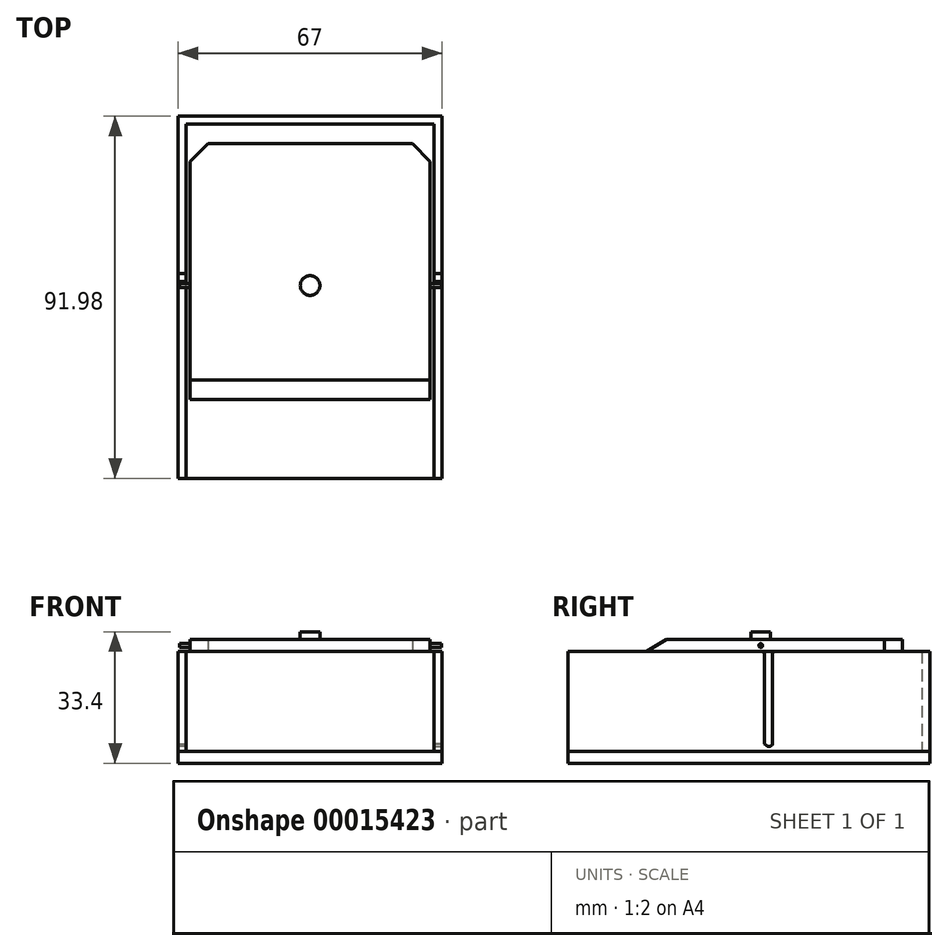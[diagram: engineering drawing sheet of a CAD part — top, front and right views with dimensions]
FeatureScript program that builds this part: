
annotation { "Feature Type Name" : "Feature", "Feature Type Description" : "" }
export const myFeature = defineFeature(function(context is Context, id is Id, definition is map)
    precondition{}
    {
        {
            var Q0;
            Q0=qCreatedBy(makeId("Top.planeOp"),FACE);
            var sketch = newSketch(context, id + "F0", { "sketchPlane" : qUnion([Q0])});
            skLineSegment(sketch, "E0.bottom", {"start": v(-39.88, -77.5) * mm, "end": v(23.12, -77.5) * mm});
            skLineSegment(sketch, "E0.top", {"start": v(-39.88, 12.5) * mm, "end": v(23.12, 12.5) * mm});
            skLineSegment(sketch, "E0.left", {"start": v(-39.88, -77.5) * mm, "end": v(-39.88, 12.5) * mm});
            skLineSegment(sketch, "E0.right", {"start": v(23.12, -77.5) * mm, "end": v(23.12, 12.5) * mm});
            skLineSegment(sketch, "E1.bottom", {"start": v(-41.88, -77.48) * mm, "end": v(25.12, -77.48) * mm});
            skLineSegment(sketch, "E1.top", {"start": v(-41.88, 14.5) * mm, "end": v(25.12, 14.5) * mm});
            skLineSegment(sketch, "E1.left", {"start": v(-41.88, -77.48) * mm, "end": v(-41.88, 14.5) * mm});
            skLineSegment(sketch, "E1.right", {"start": v(25.12, -77.48) * mm, "end": v(25.12, 14.5) * mm});
            skSolve(sketch);
        }
        {
            var Q0;
            {var subQ7=sQuery(id+"F0.wireOp",EDGE,"E0.top");Q0=makeQuery(id+"F0.imprint","IMPRINT",FACE,{"disambiguationData":[TD([[makeQuery(id+"F0.imprint","IMPRINT",EDGE,{"derivedFrom":subQ7}),1.0]])]});}
            extrude(context, id + "F1", {"entities" : qUnion([Q0]), "depth" : 25.4 * mm});
        }
        {
            var Q0;
            Q0=makeQuery(id+"F1.opExtrude","SWEPT_FACE",FACE,{"disambiguationData":[OSD([sQuery(id+"F0.wireOp",EDGE,"E0.left")])]});
            var sketch = newSketch(context, id + "F2", { "sketchPlane" : qUnion([Q0])});
            skLineSegment(sketch, "E2", {"start": v(-25.5, 25.4) * mm, "end": v(-25.5, 1.76) * mm});
            skLineSegment(sketch, "E3", {"start": v(-25.5, 1.76) * mm, "end": v(-26.4, 0.86) * mm});
            skLineSegment(sketch, "E4", {"start": v(-26.4, 0.86) * mm, "end": v(-27.5, 1.96) * mm});
            skLineSegment(sketch, "E5", {"start": v(-27.5, 1.96) * mm, "end": v(-27.5, 25.4) * mm});
            skLineSegment(sketch, "E6", {"start": v(-27.5, 25.4) * mm, "end": v(-25.5, 25.4) * mm});
            skSolve(sketch);
        }
        {
            var Q0;
            Q0=makeQuery(id+"F2.imprint","IMPRINT",FACE,{"disambiguationData":[TD([[makeQuery(id+"F2.imprint","IMPRINT",EDGE,{"derivedFrom":sQuery(id+"F2.wireOp",EDGE,"E2")}),-1.0]])]});
            extrude(context, id + "F3", {"entities" : qUnion([Q0]), "operationType" : NewBodyOperationType.REMOVE, "oppositeDirection" : true, "depth" : 2.03 * mm});
        }
        {
            var Q0;
            Q0=qSketchRegion(id+"F2",true);
            var Q1;
            Q1=makeQuery(id+"F2.imprint","IMPRINT",FACE,{"disambiguationData":[TD([[makeQuery(id+"F2.imprint","IMPRINT",EDGE,{"derivedFrom":sQuery(id+"F2.wireOp",EDGE,"E2")}),-1.0]])]});
            extrude(context, id + "F4", {"entities" : qUnion([Q0, Q1]), "operationType" : NewBodyOperationType.REMOVE, "depth" : 77.17 * mm});
        }
        {
            var Q0;
            {var subQ0=sQuery(id+"F0.wireOp",EDGE,"E0.top");var subQ1=sQuery(id+"F0.wireOp",EDGE,"E0.left");var subQ2=sQuery(id+"F0.wireOp",EDGE,"E0.right");var subQ3=sQuery(id+"F0.wireOp",EDGE,"E1.bottom");var subQ4=sQuery(id+"F0.wireOp",EDGE,"E1.top");var subQ5=sQuery(id+"F0.wireOp",EDGE,"E1.left");var subQ6=sQuery(id+"F0.wireOp",EDGE,"E1.right");var subQ14=makeQuery(id+"F1.opExtrude","SWEPT_FACE",FACE,{"disambiguationData":[OSD([subQ0])]});Q0=makeQuery(id+"F4.boolean.opBoolean","SPLIT",FACE,{"disambiguationData":[TD([subQ14])],"derivedFrom":makeQuery(id+"F3.boolean.opBoolean","SPLIT",FACE,{"disambiguationData":[TD([subQ14])],"derivedFrom":makeQuery(id+"F1.opExtrude","CAP_FACE",FACE,{"disambiguationData":[OSD([subQ0,subQ1,subQ2,subQ3,subQ4,subQ5,subQ6])],"isStart":false})})});}
            var sketch = newSketch(context, id + "F5", { "sketchPlane" : qUnion([Q0])});
            skLineSegment(sketch, "E7", {"start": v(-34.36, 7.5) * mm, "end": v(-38.88, 2.99) * mm});
            skLineSegment(sketch, "E8", {"start": v(-38.88, 2.99) * mm, "end": v(-38.88, -57.48) * mm});
            skLineSegment(sketch, "E9", {"start": v(-38.88, -57.48) * mm, "end": v(22.12, -57.48) * mm});
            skLineSegment(sketch, "E10", {"start": v(22.12, -57.48) * mm, "end": v(22.12, 2.99) * mm});
            skLineSegment(sketch, "E11", {"start": v(22.12, 2.99) * mm, "end": v(17.6, 7.5) * mm});
            skLineSegment(sketch, "E12", {"start": v(17.6, 7.5) * mm, "end": v(-34.36, 7.5) * mm});
            skSolve(sketch);
        }
        {
            var Q0;
            Q0=makeQuery(id+"F5.imprint","IMPRINT",FACE,{"disambiguationData":[TD([[makeQuery(id+"F5.imprint","IMPRINT",EDGE,{"derivedFrom":sQuery(id+"F5.wireOp",EDGE,"E7")}),1.0]])]});
            extrude(context, id + "F6", {"entities" : qUnion([Q0]), "depth" : 3 * mm});
        }
        {
            var Q0;
            Q0=makeQuery(id+"F6.opExtrude","SWEPT_FACE",FACE,{"disambiguationData":[OSD([sQuery(id+"F5.wireOp",EDGE,"E10")])]});
            var sketch = newSketch(context, id + "F7", { "sketchPlane" : qUnion([Q0])});
            skCircle(sketch, "E13", {"center": v(-28.5, 26.9) * mm, "radius": 0.48 * mm});
            skSolve(sketch);
        }
        {
            var Q0;
            Q0=makeQuery(id+"F7.imprint","IMPRINT",FACE,{"disambiguationData":[TD([[makeQuery(id+"F7.imprint","IMPRINT",EDGE,{"derivedFrom":sQuery(id+"F7.wireOp",EDGE,"E13")}),1.0]])]});
            extrude(context, id + "F8", {"entities" : qUnion([Q0]), "operationType" : NewBodyOperationType.ADD, "depth" : 2.88 * mm});
        }
        {
            var Q0;
            Q0=makeQuery(id+"F8.opExtrude","CAP_FACE",FACE,{"disambiguationData":[OSD([sQuery(id+"F7.wireOp",EDGE,"E13")])],"isStart":false});
            extrude(context, id + "F9", {"entities" : qUnion([Q0]), "operationType" : NewBodyOperationType.ADD, "oppositeDirection" : true, "depth" : 66.56 * mm});
        }
        {
            var Q0;
            {var subQ5=sQuery(id+"F0.wireOp",EDGE,"E0.top");Q0=makeQuery(id+"F0.imprint","IMPRINT",FACE,{"disambiguationData":[TD([[makeQuery(id+"F0.imprint","IMPRINT",EDGE,{"derivedFrom":subQ5}),-1.0]])]});}
            var Q1;
            {var subQ7=sQuery(id+"F0.wireOp",EDGE,"E0.top");Q1=makeQuery(id+"F0.imprint","IMPRINT",FACE,{"disambiguationData":[TD([[makeQuery(id+"F0.imprint","IMPRINT",EDGE,{"derivedFrom":subQ7}),1.0]])]});}
            extrude(context, id + "F10", {"entities" : qUnion([Q0, Q1]), "oppositeDirection" : true, "depth" : 3 * mm});
        }
        {
            var Q0;
            Q0=makeQuery(id+"F6.opExtrude","CAP_FACE",FACE,{"disambiguationData":[OSD([sQuery(id+"F5.wireOp",EDGE,"E7"),sQuery(id+"F5.wireOp",EDGE,"E8"),sQuery(id+"F5.wireOp",EDGE,"E9"),sQuery(id+"F5.wireOp",EDGE,"E10"),sQuery(id+"F5.wireOp",EDGE,"E11"),sQuery(id+"F5.wireOp",EDGE,"E12")])],"isStart":false});
            var sketch = newSketch(context, id + "F11", { "sketchPlane" : qUnion([Q0])});
            skPoint(sketch, "E14", {"position": v(-38.88, -28.5) * mm});
            skPoint(sketch, "E15", {"position": v(22.12, -28.5) * mm});
            skLineSegment(sketch, "E16", {"start": v(-38.88, -28.5) * mm, "end": v(-8.38, -28.5) * mm});
            skLineSegment(sketch, "E17", {"start": v(-8.38, -28.5) * mm, "end": v(22.12, -28.5) * mm});
            skCircle(sketch, "E18", {"center": v(-8.38, -28.5) * mm, "radius": 2.5 * mm});
            skCircle(sketch, "E19", {"center": v(-8.38, -28.5) * mm, "radius": 3.57 * mm});
            skSolve(sketch);
        }
        {
            var Q0;
            {var subQ1=sQuery(id+"F11.wireOp",EDGE,"E17");var subQ3=sQuery(id+"F11.wireOp",EDGE,"E16");var subQ5=makeQuery(id+"F11.imprint","INTERSECT",VERTEX,{"derivedFrom":[subQ3,subQ1]});Q0=makeQuery(id+"F11.imprint","IMPRINT",FACE,{"disambiguationData":[TD([[makeQuery(id+"F11.imprint","IMPRINT",EDGE,{"disambiguationData":[TD([[subQ5,1.0]])],"derivedFrom":subQ3}),1.0]])]});}
            var Q1;
            {var subQ1=sQuery(id+"F11.wireOp",EDGE,"E17");var subQ3=sQuery(id+"F11.wireOp",EDGE,"E16");var subQ5=makeQuery(id+"F11.imprint","INTERSECT",VERTEX,{"derivedFrom":[subQ3,subQ1]});Q1=makeQuery(id+"F11.imprint","IMPRINT",FACE,{"disambiguationData":[TD([[makeQuery(id+"F11.imprint","IMPRINT",EDGE,{"disambiguationData":[TD([[subQ5,1.0]])],"derivedFrom":subQ3}),-1.0]])]});}
            extrude(context, id + "F12", {"entities" : qUnion([Q0, Q1]), "operationType" : NewBodyOperationType.ADD, "depth" : 2 * mm});
        }
        {
            var Q0;
            Q0=makeQuery(id+"F4.boolean.opBoolean","COPY",EDGE,{"derivedFrom":makeQuery(id+"F4.opExtrude","SWEPT_EDGE",EDGE,{"disambiguationData":[OSD([sQuery(id+"F0.wireOp",EDGE,"E0.left"),sQuery(id+"F2.wireOp",EDGE,"E5"),sQuery(id+"F2.wireOp",EDGE,"E6")])]})});
            var Q1;
            Q1=makeQuery(id+"F4.boolean.opBoolean","COPY",EDGE,{"derivedFrom":makeQuery(id+"F4.opExtrude","SWEPT_EDGE",EDGE,{"disambiguationData":[OSD([sQuery(id+"F0.wireOp",EDGE,"E0.left"),sQuery(id+"F2.wireOp",EDGE,"E2"),sQuery(id+"F2.wireOp",EDGE,"E6")])]})});
            var Q2;
            Q2=makeQuery(id+"F3.boolean.opBoolean","COPY",EDGE,{"derivedFrom":makeQuery(id+"F3.opExtrude","SWEPT_EDGE",EDGE,{"disambiguationData":[OSD([sQuery(id+"F0.wireOp",EDGE,"E0.left"),sQuery(id+"F2.wireOp",EDGE,"E2"),sQuery(id+"F2.wireOp",EDGE,"E6")])]})});
            var Q3;
            Q3=makeQuery(id+"F3.boolean.opBoolean","COPY",EDGE,{"derivedFrom":makeQuery(id+"F3.opExtrude","SWEPT_EDGE",EDGE,{"disambiguationData":[OSD([sQuery(id+"F0.wireOp",EDGE,"E0.left"),sQuery(id+"F2.wireOp",EDGE,"E5"),sQuery(id+"F2.wireOp",EDGE,"E6")])]})});
            var Q4;
            Q4=makeQuery(id+"F3.boolean.opBoolean","COPY",EDGE,{"derivedFrom":makeQuery(id+"F3.opExtrude","SWEPT_EDGE",EDGE,{"disambiguationData":[OSD([sQuery(id+"F2.wireOp",EDGE,"E3"),sQuery(id+"F2.wireOp",EDGE,"E4")])]})});
            var Q5;
            Q5=makeQuery(id+"F4.boolean.opBoolean","COPY",EDGE,{"derivedFrom":makeQuery(id+"F4.opExtrude","SWEPT_EDGE",EDGE,{"disambiguationData":[OSD([sQuery(id+"F2.wireOp",EDGE,"E3"),sQuery(id+"F2.wireOp",EDGE,"E4")])]})});
            fillet(context, id + "F13", {"entities" : qUnion([Q0, Q1, Q2, Q3, Q4, Q5]), "radius" : 1 * mm, "tangentPropagation" : true, "allowEdgeOverflow" : false});
        }
        {
            var Q0;
            Q0=makeQuery(id+"F6.opExtrude","CAP_EDGE",EDGE,{"disambiguationData":[OSD([sQuery(id+"F5.wireOp",EDGE,"E9")])],"isStart":false});
            chamfer(context, id + "F14", {"entities" : qUnion([Q0]), "chamferType" : ChamferType.TWO_OFFSETS, "width1" : 5 * mm, "oppositeDirection" : false, "width2" : 3 * mm, "tangentPropagation" : true});
        }
    });
